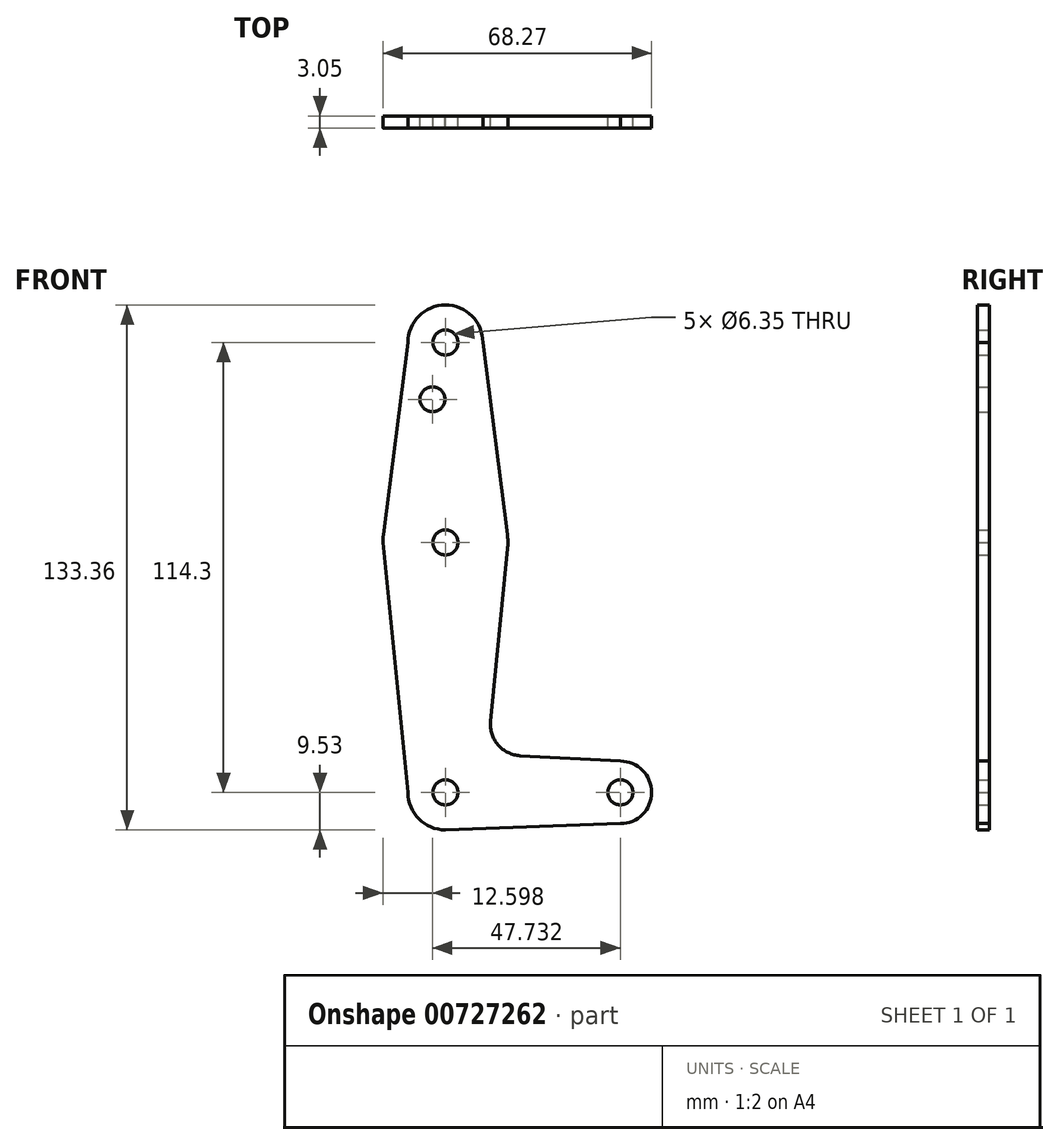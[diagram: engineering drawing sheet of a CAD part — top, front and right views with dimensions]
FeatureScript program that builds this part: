
annotation { "Feature Type Name" : "Feature", "Feature Type Description" : "" }
export const myFeature = defineFeature(function(context is Context, id is Id, definition is map)
    precondition{}
    {
        {
            var Q0;
            Q0=qCreatedBy(makeId("Front.planeOp"),FACE);
            var sketch = newSketch(context, id + "F0", { "sketchPlane" : qUnion([Q0])});
            skLineSegment(sketch, "E0", {"start": v(44.45, 0) * mm, "end": v(0, 0) * mm});
            skLineSegment(sketch, "E1", {"start": v(0, 0) * mm, "end": v(0, 63.5) * mm});
            skLineSegment(sketch, "E2", {"start": v(0, 63.5) * mm, "end": v(0, 114.3) * mm});
            skCircle(sketch, "E3", {"center": v(0, 114.3) * mm, "radius": 9.53 * mm});
            skCircle(sketch, "E4", {"center": v(0, 63.5) * mm, "radius": 15.88 * mm});
            skCircle(sketch, "E5", {"center": v(0, 0) * mm, "radius": 9.53 * mm});
            skCircle(sketch, "E6", {"center": v(44.45, 0) * mm, "radius": 7.94 * mm});
            skLineSegment(sketch, "E7", {"start": v(-9.53, 114.3) * mm, "end": v(-15.75, 65.5) * mm});
            skLineSegment(sketch, "E8", {"start": v(9.53, 114.3) * mm, "end": v(15.75, 65.5) * mm});
            skPoint(sketch, "E9.startSnap0", {"position": v(22.23, 0) * mm});
            skLineSegment(sketch, "E10", {"start": v(0, -9.53) * mm, "end": v(44.45, -7.94) * mm});
            skLineSegment(sketch, "E11", {"start": v(18.95, 9.33) * mm, "end": v(44.45, 7.94) * mm});
            skLineSegment(sketch, "E12", {"start": v(-9.52, 0) * mm, "end": v(-15.88, 63.5) * mm});
            skLineSegment(sketch, "E13", {"start": v(11.47, 18.05) * mm, "end": v(15.95, 63.5) * mm});
            skCircle(sketch, "E14", {"center": v(0, 63.5) * mm, "radius": 3.18 * mm});
            skCircle(sketch, "E15", {"center": v(0, 114.3) * mm, "radius": 3.18 * mm});
            skCircle(sketch, "E16", {"center": v(-3.28, 99.88) * mm, "radius": 3.18 * mm});
            skCircle(sketch, "E17", {"center": v(0, 0) * mm, "radius": 3.18 * mm});
            skCircle(sketch, "E18", {"center": v(44.45, 0) * mm, "radius": 3.18 * mm});
            skPoint(sketch, "E19.newPointB", {"position": v(9.7, 0) * mm});
            skArc(sketch, "E19.filletArc", {"start": v(11.47, 18.05) * mm, "mid": v(13.35, 12.09) * mm, "end": v(18.95, 9.33) * mm});
            skSolve(sketch);
        }
        {
            var Q0;
            Q0=makeQuery(id+"F0.imprint","IMPRINT",FACE,{"disambiguationData":[TD([[makeQuery(id+"F0.imprint","IMPRINT",EDGE,{"derivedFrom":sQuery(id+"F0.wireOp",EDGE,"E15")}),-1.0]])]});
            var Q1;
            {var subQ0=sQuery(id+"F0.wireOp",EDGE,"E7");Q1=makeQuery(id+"F0.imprint","IMPRINT",FACE,{"disambiguationData":[TD([[makeQuery(id+"F0.imprint","IMPRINT",EDGE,{"derivedFrom":subQ0}),1.0]])]});}
            var Q2;
            {var subQ5=sQuery(id+"F0.wireOp",EDGE,"E8");Q2=makeQuery(id+"F0.imprint","IMPRINT",FACE,{"disambiguationData":[TD([[makeQuery(id+"F0.imprint","IMPRINT",EDGE,{"derivedFrom":subQ5}),-1.0]])]});}
            var Q3;
            {var subQ0=sQuery(id+"F0.wireOp",EDGE,"E4");var subQ2=sQuery(id+"F0.wireOp",EDGE,"E1");var subQ3=makeQuery(id+"F0.imprint","INTERSECT",VERTEX,{"derivedFrom":[subQ2,subQ0]});Q3=makeQuery(id+"F0.imprint","IMPRINT",FACE,{"disambiguationData":[TD([[makeQuery(id+"F0.imprint","IMPRINT",EDGE,{"disambiguationData":[TD([[subQ3,-1.0]])],"derivedFrom":subQ2}),-1.0]])]});}
            var Q4;
            {var subQ0=sQuery(id+"F0.wireOp",EDGE,"E4");var subQ5=sQuery(id+"F0.wireOp",EDGE,"E1");var subQ10=makeQuery(id+"F0.imprint","INTERSECT",VERTEX,{"derivedFrom":[subQ5,subQ0]});Q4=makeQuery(id+"F0.imprint","IMPRINT",FACE,{"disambiguationData":[TD([[makeQuery(id+"F0.imprint","IMPRINT",EDGE,{"disambiguationData":[TD([[subQ10,-1.0]])],"derivedFrom":subQ5}),1.0]])]});}
            var Q5;
            {var subQ0=sQuery(id+"F0.wireOp",EDGE,"E5");var subQ1=sQuery(id+"F0.wireOp",EDGE,"E1");var subQ2=makeQuery(id+"F0.imprint","INTERSECT",VERTEX,{"derivedFrom":[subQ1,subQ0]});Q5=makeQuery(id+"F0.imprint","IMPRINT",FACE,{"disambiguationData":[TD([[makeQuery(id+"F0.imprint","IMPRINT",EDGE,{"disambiguationData":[TD([[subQ2,-1.0]])],"derivedFrom":subQ1}),1.0]])]});}
            var Q6;
            {var subQ11=sQuery(id+"F0.wireOp",EDGE,"E11");Q6=makeQuery(id+"F0.imprint","IMPRINT",FACE,{"disambiguationData":[TD([[makeQuery(id+"F0.imprint","IMPRINT",EDGE,{"derivedFrom":subQ11}),-1.0]])]});}
            var Q7;
            {var subQ1=sQuery(id+"F0.wireOp",EDGE,"E5");var subQ4=sQuery(id+"F0.wireOp",EDGE,"E0");var subQ5=makeQuery(id+"F0.imprint","INTERSECT",VERTEX,{"derivedFrom":[subQ4,subQ1]});Q7=makeQuery(id+"F0.imprint","IMPRINT",FACE,{"disambiguationData":[TD([[makeQuery(id+"F0.imprint","IMPRINT",EDGE,{"disambiguationData":[TD([[subQ5,-1.0]])],"derivedFrom":subQ4}),1.0]])]});}
            var Q8;
            {var subQ0=sQuery(id+"F0.wireOp",EDGE,"E5");var subQ1=sQuery(id+"F0.wireOp",EDGE,"E0");var subQ2=makeQuery(id+"F0.imprint","INTERSECT",VERTEX,{"derivedFrom":[subQ1,subQ0]});Q8=makeQuery(id+"F0.imprint","IMPRINT",FACE,{"disambiguationData":[TD([[makeQuery(id+"F0.imprint","IMPRINT",EDGE,{"disambiguationData":[TD([[subQ2,-1.0]])],"derivedFrom":subQ1}),-1.0]])]});}
            var Q9;
            {var subQ0=sQuery(id+"F0.wireOp",EDGE,"E6");var subQ1=sQuery(id+"F0.wireOp",EDGE,"E0");var subQ2=makeQuery(id+"F0.imprint","INTERSECT",VERTEX,{"derivedFrom":[subQ1,subQ0]});Q9=makeQuery(id+"F0.imprint","IMPRINT",FACE,{"disambiguationData":[TD([[makeQuery(id+"F0.imprint","IMPRINT",EDGE,{"disambiguationData":[TD([[subQ2,-1.0]])],"derivedFrom":subQ1}),1.0]])]});}
            var Q10;
            Q10=makeQuery(id+"F0.imprint","IMPRINT",FACE,{"disambiguationData":[TD([[makeQuery(id+"F0.imprint","IMPRINT",EDGE,{"derivedFrom":sQuery(id+"F0.wireOp",EDGE,"E18")}),-1.0]])]});
            extrude(context, id + "F1", {"entities" : qUnion([Q0, Q1, Q2, Q3, Q4, Q5, Q6, Q7, Q8, Q9, Q10]), "depth" : 3.05 * mm, "offsetDistance" : 25.4 * mm});
        }
    });
